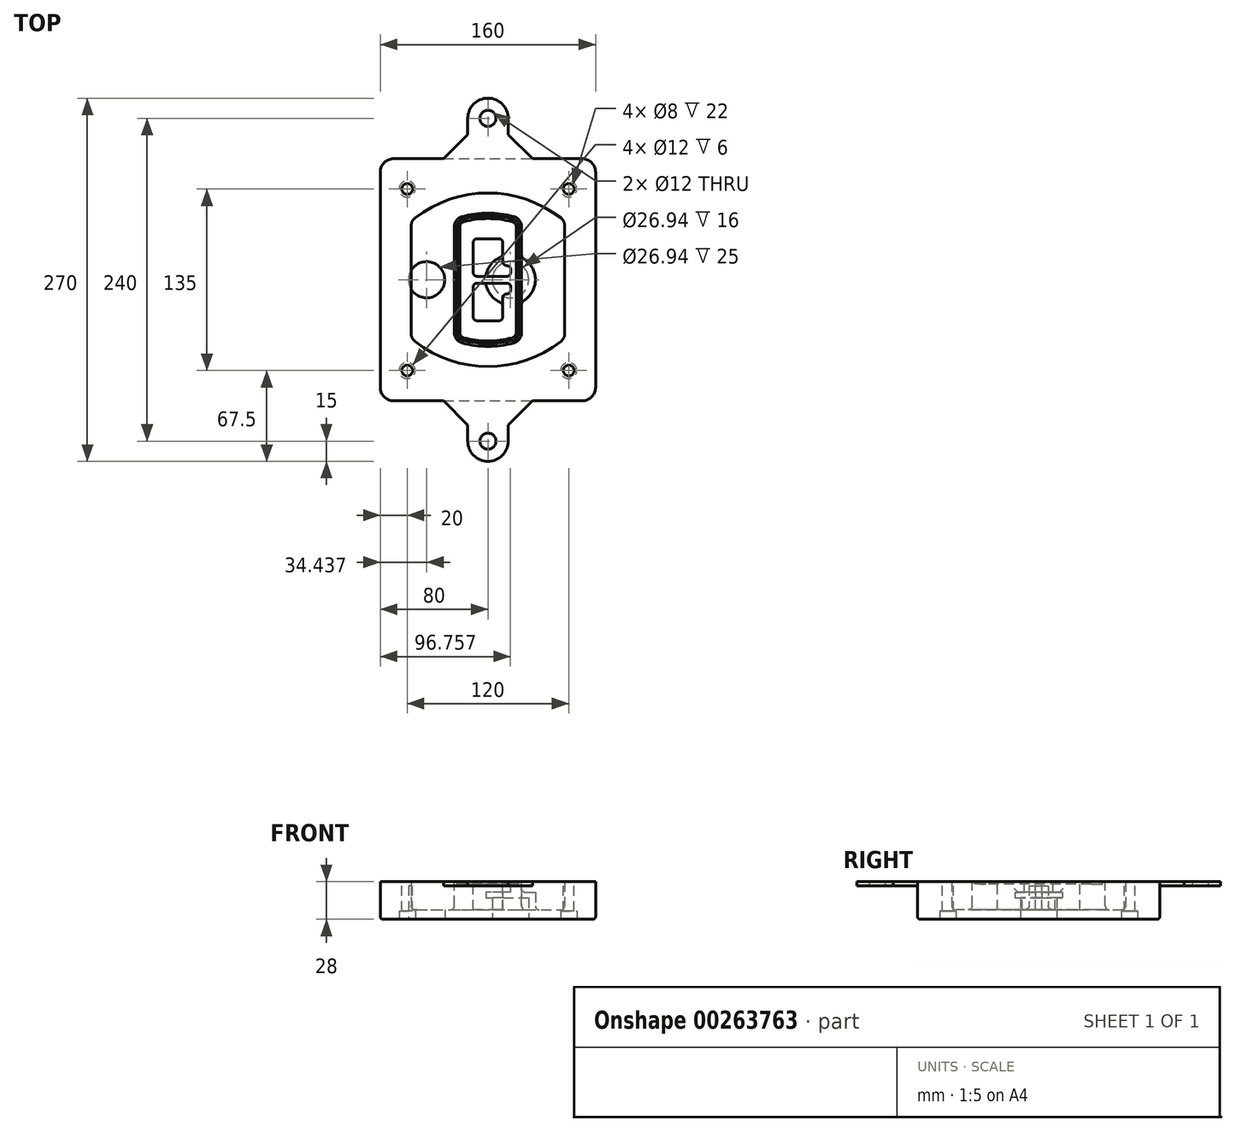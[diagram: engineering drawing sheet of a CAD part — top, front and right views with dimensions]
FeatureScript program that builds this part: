
annotation { "Feature Type Name" : "Feature", "Feature Type Description" : "" }
export const myFeature = defineFeature(function(context is Context, id is Id, definition is map)
    precondition{}
    {
        {
            var Q0;
            Q0=qCreatedBy(makeId("Top.planeOp"),FACE);
            var sketch = newSketch(context, id + "F0", { "sketchPlane" : qUnion([Q0])});
            skPoint(sketch, "E0.rect.middle", {"position": v(0, 0) * mm});
            skLineSegment(sketch, "E1.bottom", {"start": v(-70, -90) * mm, "end": v(70, -90) * mm});
            skLineSegment(sketch, "E1.top", {"start": v(-70, 90) * mm, "end": v(70, 90) * mm});
            skLineSegment(sketch, "E1.left", {"start": v(-80, -80) * mm, "end": v(-80, 80) * mm});
            skLineSegment(sketch, "E1.right", {"start": v(80, -80) * mm, "end": v(80, 80) * mm});
            skLineSegment(sketch, "E2", {"start": v(-80, 90) * mm, "end": v(80, -90) * mm, "construction": true});
            skLineSegment(sketch, "E3", {"start": v(80, 90) * mm, "end": v(-80, -90) * mm, "construction": true});
            skCircle(sketch, "E4", {"center": v(-60, 67.5) * mm, "radius": 4 * mm});
            skCircle(sketch, "E5", {"center": v(60, 67.5) * mm, "radius": 4 * mm});
            skCircle(sketch, "E6", {"center": v(60, -67.5) * mm, "radius": 4 * mm});
            skCircle(sketch, "E7", {"center": v(-60, -67.5) * mm, "radius": 4 * mm});
            skLineSegment(sketch, "E8", {"start": v(-60, 67.5) * mm, "end": v(60, 67.5) * mm, "construction": true});
            skLineSegment(sketch, "E9", {"start": v(60, 67.5) * mm, "end": v(60, -67.5) * mm, "construction": true});
            skLineSegment(sketch, "E10", {"start": v(60, -67.5) * mm, "end": v(-60, -67.5) * mm, "construction": true});
            skLineSegment(sketch, "E11", {"start": v(-60, -67.5) * mm, "end": v(-60, 67.5) * mm, "construction": true});
            skLineSegment(sketch, "E12", {"start": v(-60, 40.3) * mm, "end": v(-60, -40.3) * mm});
            skLineSegment(sketch, "E13", {"start": v(60, 40.3) * mm, "end": v(60, -40.3) * mm});
            skArc(sketch, "E14", {"start": v(56.15, 48.18) * mm, "mid": v(0, 67.5) * mm, "end": v(-56.15, 48.18) * mm});
            skArc(sketch, "E15", {"start": v(-56.15, -48.18) * mm, "mid": v(0, -67.5) * mm, "end": v(56.15, -48.18) * mm});
            skLineSegment(sketch, "E16", {"start": v(-60, 0) * mm, "end": v(60, 0) * mm, "construction": true});
            skPoint(sketch, "E17.visualSharp", {"position": v(-60, -45) * mm});
            skArc(sketch, "E17.filletArc", {"start": v(-60, -40.3) * mm, "mid": v(-58.99, -44.68) * mm, "end": v(-56.15, -48.18) * mm});
            skPoint(sketch, "E18.visualSharp", {"position": v(-60, 45) * mm});
            skArc(sketch, "E18.filletArc", {"start": v(-56.15, 48.18) * mm, "mid": v(-58.99, 44.68) * mm, "end": v(-60, 40.3) * mm});
            skPoint(sketch, "E19.visualSharp", {"position": v(60, 45) * mm});
            skArc(sketch, "E19.filletArc", {"start": v(60, 40.3) * mm, "mid": v(58.99, 44.68) * mm, "end": v(56.15, 48.18) * mm});
            skPoint(sketch, "E20.visualSharp", {"position": v(60, -45) * mm});
            skArc(sketch, "E20.filletArc", {"start": v(56.15, -48.18) * mm, "mid": v(58.99, -44.68) * mm, "end": v(60, -40.3) * mm});
            skPoint(sketch, "E21.visualSharp", {"position": v(-80, 90) * mm});
            skArc(sketch, "E21.filletArc", {"start": v(-70, 90) * mm, "mid": v(-77.07, 87.07) * mm, "end": v(-80, 80) * mm});
            skPoint(sketch, "E22.visualSharp", {"position": v(80, 90) * mm});
            skArc(sketch, "E22.filletArc", {"start": v(80, 80) * mm, "mid": v(77.07, 87.07) * mm, "end": v(70, 90) * mm});
            skPoint(sketch, "E23.visualSharp", {"position": v(80, -90) * mm});
            skArc(sketch, "E23.filletArc", {"start": v(70, -90) * mm, "mid": v(77.07, -87.07) * mm, "end": v(80, -80) * mm});
            skPoint(sketch, "E24.visualSharp", {"position": v(-80, -90) * mm});
            skArc(sketch, "E24.filletArc", {"start": v(-80, -80) * mm, "mid": v(-77.07, -87.07) * mm, "end": v(-70, -90) * mm});
            skArc(sketch, "E25.0", {"start": v(57, 40.3) * mm, "mid": v(56.3, 43.36) * mm, "end": v(54.3, 45.81) * mm});
            skLineSegment(sketch, "E25.1", {"start": v(57, 40.3) * mm, "end": v(57, -40.3) * mm});
            skArc(sketch, "E25.2", {"start": v(54.3, -45.81) * mm, "mid": v(56.3, -43.36) * mm, "end": v(57, -40.3) * mm});
            skArc(sketch, "E25.3", {"start": v(-54.3, -45.81) * mm, "mid": v(0, -64.5) * mm, "end": v(54.3, -45.81) * mm});
            skArc(sketch, "E25.4", {"start": v(-57, -40.3) * mm, "mid": v(-56.3, -43.36) * mm, "end": v(-54.3, -45.81) * mm});
            skArc(sketch, "E25.5", {"start": v(54.3, 45.81) * mm, "mid": v(0, 64.5) * mm, "end": v(-54.3, 45.81) * mm});
            skLineSegment(sketch, "E25.6", {"start": v(-57, 40.3) * mm, "end": v(-57, -40.3) * mm});
            skArc(sketch, "E25.7", {"start": v(-54.3, 45.81) * mm, "mid": v(-56.3, 43.36) * mm, "end": v(-57, 40.3) * mm});
            skArc(sketch, "E26.0", {"start": v(-58.62, 51.33) * mm, "mid": v(-62.58, 46.43) * mm, "end": v(-64, 40.3) * mm});
            skArc(sketch, "E26.1", {"start": v(58.62, 51.33) * mm, "mid": v(0, 71.5) * mm, "end": v(-58.62, 51.33) * mm});
            skArc(sketch, "E26.2", {"start": v(64, 40.3) * mm, "mid": v(62.58, 46.43) * mm, "end": v(58.62, 51.33) * mm});
            skLineSegment(sketch, "E26.3", {"start": v(64, 40.3) * mm, "end": v(64, -40.3) * mm});
            skArc(sketch, "E26.4", {"start": v(58.62, -51.33) * mm, "mid": v(62.58, -46.43) * mm, "end": v(64, -40.3) * mm});
            skLineSegment(sketch, "E26.5", {"start": v(-64, 40.3) * mm, "end": v(-64, -40.3) * mm});
            skArc(sketch, "E26.6", {"start": v(-58.62, -51.33) * mm, "mid": v(0, -71.5) * mm, "end": v(58.62, -51.33) * mm});
            skArc(sketch, "E26.7", {"start": v(-64, -40.3) * mm, "mid": v(-62.58, -46.43) * mm, "end": v(-58.62, -51.33) * mm});
            skSolve(sketch);
        }
        {
            var Q0;
            Q0=makeQuery(id+"F0.imprint","IMPRINT",FACE,{"disambiguationData":[TD([[makeQuery(id+"F0.imprint","IMPRINT",EDGE,{"derivedFrom":sQuery(id+"F0.wireOp",EDGE,"E1.bottom")}),1.0]])]});
            var Q1;
            Q1=makeQuery(id+"F0.imprint","IMPRINT",FACE,{"disambiguationData":[TD([[makeQuery(id+"F0.imprint","IMPRINT",EDGE,{"derivedFrom":sQuery(id+"F0.wireOp",EDGE,"E12")}),1.0]])]});
            var Q2;
            Q2=makeQuery(id+"F0.imprint","IMPRINT",FACE,{"disambiguationData":[TD([[makeQuery(id+"F0.imprint","IMPRINT",EDGE,{"derivedFrom":sQuery(id+"F0.wireOp",EDGE,"E25.0")}),1.0]])]});
            var Q3;
            Q3=makeQuery(id+"F0.imprint","IMPRINT",FACE,{"disambiguationData":[TD([[makeQuery(id+"F0.imprint","IMPRINT",EDGE,{"derivedFrom":sQuery(id+"F0.wireOp",EDGE,"E12")}),-1.0]])]});
            extrude(context, id + "F1", {"entities" : qUnion([Q0, Q1, Q2, Q3]), "oppositeDirection" : true, "depth" : 25 * mm});
        }
        {
            var Q0;
            Q0=makeQuery(id+"F0.imprint","IMPRINT",FACE,{"disambiguationData":[TD([[makeQuery(id+"F0.imprint","IMPRINT",EDGE,{"derivedFrom":sQuery(id+"F0.wireOp",EDGE,"E12")}),1.0]])]});
            extrude(context, id + "F2", {"entities" : qUnion([Q0]), "operationType" : NewBodyOperationType.ADD, "depth" : 3 * mm});
        }
        {
            var Q0;
            Q0=makeQuery(id+"F0.imprint","IMPRINT",FACE,{"disambiguationData":[TD([[makeQuery(id+"F0.imprint","IMPRINT",EDGE,{"derivedFrom":sQuery(id+"F0.wireOp",EDGE,"E25.0")}),1.0]])]});
            extrude(context, id + "F3", {"entities" : qUnion([Q0]), "operationType" : NewBodyOperationType.REMOVE, "oppositeDirection" : true, "depth" : 18 * mm});
        }
        {
            var Q0;
            Q0=makeQuery(id+"F2.opExtrude","CAP_FACE",FACE,{"disambiguationData":[OSD([sQuery(id+"F0.wireOp",EDGE,"E12"),sQuery(id+"F0.wireOp",EDGE,"E13"),sQuery(id+"F0.wireOp",EDGE,"E14"),sQuery(id+"F0.wireOp",EDGE,"E15"),sQuery(id+"F0.wireOp",EDGE,"E17.filletArc"),sQuery(id+"F0.wireOp",EDGE,"E18.filletArc"),sQuery(id+"F0.wireOp",EDGE,"E19.filletArc"),sQuery(id+"F0.wireOp",EDGE,"E20.filletArc"),sQuery(id+"F0.wireOp",EDGE,"E25.0"),sQuery(id+"F0.wireOp",EDGE,"E25.1"),sQuery(id+"F0.wireOp",EDGE,"E25.2"),sQuery(id+"F0.wireOp",EDGE,"E25.3"),sQuery(id+"F0.wireOp",EDGE,"E25.4"),sQuery(id+"F0.wireOp",EDGE,"E25.5"),sQuery(id+"F0.wireOp",EDGE,"E25.6"),sQuery(id+"F0.wireOp",EDGE,"E25.7")])],"isStart":false});
            var sketch = newSketch(context, id + "F4", { "sketchPlane" : qUnion([Q0])});
            skArc(sketch, "E27.0", {"start": v(-19.08, -46.97) * mm, "mid": v(0, -49.5) * mm, "end": v(19.08, -46.97) * mm});
            skArc(sketch, "E28.0", {"start": v(19.08, 46.97) * mm, "mid": v(0, 49.5) * mm, "end": v(-19.08, 46.97) * mm});
            skLineSegment(sketch, "E29", {"start": v(-25, 39.25) * mm, "end": v(-25, -39.25) * mm});
            skLineSegment(sketch, "E30", {"start": v(25, 39.25) * mm, "end": v(25, -39.25) * mm});
            skLineSegment(sketch, "E31", {"start": v(-25, 45.1) * mm, "end": v(25, 45.1) * mm, "construction": true});
            skLineSegment(sketch, "E32", {"start": v(-25, -45.1) * mm, "end": v(25, -45.1) * mm, "construction": true});
            skPoint(sketch, "E33.visualSharp", {"position": v(-25, 45.1) * mm});
            skArc(sketch, "E33.filletArc", {"start": v(-19.08, 46.97) * mm, "mid": v(-23.35, 44.11) * mm, "end": v(-25, 39.25) * mm});
            skPoint(sketch, "E34.visualSharp", {"position": v(25, 45.1) * mm});
            skArc(sketch, "E34.filletArc", {"start": v(25, 39.25) * mm, "mid": v(23.35, 44.11) * mm, "end": v(19.08, 46.97) * mm});
            skPoint(sketch, "E35.visualSharp", {"position": v(25, -45.1) * mm});
            skArc(sketch, "E35.filletArc", {"start": v(19.08, -46.97) * mm, "mid": v(23.35, -44.11) * mm, "end": v(25, -39.25) * mm});
            skPoint(sketch, "E36.visualSharp", {"position": v(-25, -45.1) * mm});
            skArc(sketch, "E36.filletArc", {"start": v(-25, -39.25) * mm, "mid": v(-23.35, -44.11) * mm, "end": v(-19.08, -46.97) * mm});
            skArc(sketch, "E37.0", {"start": v(54.3, 45.81) * mm, "mid": v(0, 64.5) * mm, "end": v(-54.3, 45.81) * mm});
            skArc(sketch, "E37.1", {"start": v(-54.3, 45.81) * mm, "mid": v(-56.3, 43.36) * mm, "end": v(-57, 40.3) * mm});
            skLineSegment(sketch, "E37.2", {"start": v(-57, 40.3) * mm, "end": v(-57, -40.3) * mm});
            skArc(sketch, "E37.3", {"start": v(-57, -40.3) * mm, "mid": v(-56.3, -43.36) * mm, "end": v(-54.3, -45.81) * mm});
            skArc(sketch, "E37.4", {"start": v(-54.3, -45.81) * mm, "mid": v(0, -64.5) * mm, "end": v(54.3, -45.81) * mm});
            skArc(sketch, "E37.5", {"start": v(54.3, -45.81) * mm, "mid": v(56.3, -43.36) * mm, "end": v(57, -40.3) * mm});
            skLineSegment(sketch, "E37.6", {"start": v(57, 40.3) * mm, "end": v(57, -40.3) * mm});
            skArc(sketch, "E37.7", {"start": v(57, 40.3) * mm, "mid": v(56.3, 43.36) * mm, "end": v(54.3, 45.81) * mm});
            skLineSegment(sketch, "E38.0", {"start": v(23, 39.25) * mm, "end": v(23, -39.25) * mm});
            skArc(sketch, "E38.1", {"start": v(18.56, -45.04) * mm, "mid": v(21.76, -42.9) * mm, "end": v(23, -39.25) * mm});
            skArc(sketch, "E38.2", {"start": v(-18.56, -45.04) * mm, "mid": v(0, -47.5) * mm, "end": v(18.56, -45.04) * mm});
            skArc(sketch, "E38.3", {"start": v(-23, -39.25) * mm, "mid": v(-21.76, -42.9) * mm, "end": v(-18.56, -45.04) * mm});
            skLineSegment(sketch, "E38.4", {"start": v(-23, 39.25) * mm, "end": v(-23, -39.25) * mm});
            skArc(sketch, "E38.5", {"start": v(23, 39.25) * mm, "mid": v(21.76, 42.9) * mm, "end": v(18.56, 45.04) * mm});
            skArc(sketch, "E38.6", {"start": v(-18.56, 45.04) * mm, "mid": v(-21.76, 42.9) * mm, "end": v(-23, 39.25) * mm});
            skArc(sketch, "E38.7", {"start": v(18.56, 45.04) * mm, "mid": v(0, 47.5) * mm, "end": v(-18.56, 45.04) * mm});
            skArc(sketch, "E39.0", {"start": v(21, 39.25) * mm, "mid": v(20.18, 41.68) * mm, "end": v(18.04, 43.1) * mm});
            skLineSegment(sketch, "E39.1", {"start": v(21, 39.25) * mm, "end": v(21, -39.25) * mm});
            skArc(sketch, "E39.2", {"start": v(18.04, -43.1) * mm, "mid": v(20.18, -41.68) * mm, "end": v(21, -39.25) * mm});
            skArc(sketch, "E39.3", {"start": v(-18.04, -43.1) * mm, "mid": v(0, -45.5) * mm, "end": v(18.04, -43.1) * mm});
            skArc(sketch, "E39.4", {"start": v(-21, -39.25) * mm, "mid": v(-20.18, -41.68) * mm, "end": v(-18.04, -43.1) * mm});
            skArc(sketch, "E39.5", {"start": v(18.04, 43.1) * mm, "mid": v(0, 45.5) * mm, "end": v(-18.04, 43.1) * mm});
            skLineSegment(sketch, "E39.6", {"start": v(-21, 39.25) * mm, "end": v(-21, -39.25) * mm});
            skArc(sketch, "E39.7", {"start": v(-18.04, 43.1) * mm, "mid": v(-20.18, 41.68) * mm, "end": v(-21, 39.25) * mm});
            skLineSegment(sketch, "E40", {"start": v(-25, 0) * mm, "end": v(25, 0) * mm, "construction": true});
            skLineSegment(sketch, "E41", {"start": v(-11, 5.5) * mm, "end": v(-11, 27.5) * mm});
            skLineSegment(sketch, "E42", {"start": v(-8, 30.5) * mm, "end": v(8, 30.5) * mm});
            skLineSegment(sketch, "E43", {"start": v(11, 27.5) * mm, "end": v(11, 13.5) * mm});
            skLineSegment(sketch, "E44", {"start": v(14, 10.5) * mm, "end": v(14, 10.5) * mm});
            skLineSegment(sketch, "E45", {"start": v(17, 7.5) * mm, "end": v(17, 5.5) * mm});
            skLineSegment(sketch, "E46", {"start": v(14, 2.5) * mm, "end": v(-8, 2.5) * mm});
            skPoint(sketch, "E47.visualSharp", {"position": v(-11, 30.5) * mm});
            skArc(sketch, "E47.filletArc", {"start": v(-8, 30.5) * mm, "mid": v(-10.12, 29.62) * mm, "end": v(-11, 27.5) * mm});
            skPoint(sketch, "E48.visualSharp", {"position": v(11, 30.5) * mm});
            skArc(sketch, "E48.filletArc", {"start": v(11, 27.5) * mm, "mid": v(10.12, 29.62) * mm, "end": v(8, 30.5) * mm});
            skPoint(sketch, "E49.visualSharp", {"position": v(11, 10.5) * mm});
            skArc(sketch, "E49.filletArc", {"start": v(11, 13.5) * mm, "mid": v(11.88, 11.38) * mm, "end": v(14, 10.5) * mm});
            skPoint(sketch, "E50.visualSharp", {"position": v(17, 10.5) * mm});
            skArc(sketch, "E50.filletArc", {"start": v(17, 7.5) * mm, "mid": v(16.12, 9.62) * mm, "end": v(14, 10.5) * mm});
            skPoint(sketch, "E51.visualSharp", {"position": v(17, 2.5) * mm});
            skArc(sketch, "E51.filletArc", {"start": v(14, 2.5) * mm, "mid": v(16.12, 3.38) * mm, "end": v(17, 5.5) * mm});
            skPoint(sketch, "E52.visualSharp", {"position": v(-11, 2.5) * mm});
            skArc(sketch, "E52.filletArc", {"start": v(-11, 5.5) * mm, "mid": v(-10.12, 3.38) * mm, "end": v(-8, 2.5) * mm});
            skLineSegment(sketch, "E53.0.MirrorCS", {"start": v(14, -2.5) * mm, "end": v(-8, -2.5) * mm});
            skArc(sketch, "E54.0.MirrorCS", {"start": v(-11, -5.5) * mm, "mid": v(-10.12, -3.38) * mm, "end": v(-8, -2.5) * mm});
            skLineSegment(sketch, "E55.0.MirrorCS", {"start": v(-11, -5.5) * mm, "end": v(-11, -27.5) * mm});
            skArc(sketch, "E56.0.MirrorCS", {"start": v(-8, -30.5) * mm, "mid": v(-10.12, -29.62) * mm, "end": v(-11, -27.5) * mm});
            skLineSegment(sketch, "E57.0.MirrorCS", {"start": v(-8, -30.5) * mm, "end": v(8, -30.5) * mm});
            skArc(sketch, "E58.0.MirrorCS", {"start": v(11, -27.5) * mm, "mid": v(10.12, -29.62) * mm, "end": v(8, -30.5) * mm});
            skLineSegment(sketch, "E59.0.MirrorCS", {"start": v(11, -27.5) * mm, "end": v(11, -13.5) * mm});
            skArc(sketch, "E60.0.MirrorCS", {"start": v(11, -13.5) * mm, "mid": v(11.88, -11.38) * mm, "end": v(14, -10.5) * mm});
            skArc(sketch, "E61.0.MirrorCS", {"start": v(17, -7.5) * mm, "mid": v(16.12, -9.62) * mm, "end": v(14, -10.5) * mm});
            skLineSegment(sketch, "E62.0.MirrorCS", {"start": v(17, -7.5) * mm, "end": v(17, -5.5) * mm});
            skArc(sketch, "E63.0.MirrorCS", {"start": v(14, -2.5) * mm, "mid": v(16.12, -3.38) * mm, "end": v(17, -5.5) * mm});
            skSolve(sketch);
        }
        {
            var Q0;
            Q0=makeQuery(id+"F4.imprint","IMPRINT",FACE,{"disambiguationData":[TD([[makeQuery(id+"F4.imprint","IMPRINT",EDGE,{"derivedFrom":sQuery(id+"F4.wireOp",EDGE,"E27.0")}),1.0]])]});
            var Q1;
            Q1=makeQuery(id+"F4.imprint","IMPRINT",FACE,{"disambiguationData":[TD([[makeQuery(id+"F4.imprint","IMPRINT",EDGE,{"derivedFrom":sQuery(id+"F4.wireOp",EDGE,"E38.0")}),-1.0]])]});
            var Q2;
            Q2=makeQuery(id+"F4.imprint","IMPRINT",FACE,{"disambiguationData":[TD([[makeQuery(id+"F4.imprint","IMPRINT",EDGE,{"derivedFrom":sQuery(id+"F4.wireOp",EDGE,"E39.0")}),1.0]])]});
            extrude(context, id + "F5", {"entities" : qUnion([Q0, Q1, Q2]), "operationType" : NewBodyOperationType.ADD, "endBound" : BoundingType.UP_TO_NEXT, "oppositeDirection" : true, "depth" : 25 * mm});
        }
        {
            var Q0;
            Q0=makeQuery(id+"F4.imprint","IMPRINT",FACE,{"disambiguationData":[TD([[makeQuery(id+"F4.imprint","IMPRINT",EDGE,{"derivedFrom":sQuery(id+"F4.wireOp",EDGE,"E38.0")}),-1.0]])]});
            extrude(context, id + "F6", {"entities" : qUnion([Q0]), "operationType" : NewBodyOperationType.REMOVE, "oppositeDirection" : true, "depth" : 2 * mm});
        }
        {
            var Q0;
            Q0=makeQuery(id+"F1.opExtrude","CAP_FACE",FACE,{"disambiguationData":[OSD([sQuery(id+"F0.wireOp",EDGE,"E1.bottom"),sQuery(id+"F0.wireOp",EDGE,"E1.top"),sQuery(id+"F0.wireOp",EDGE,"E1.left"),sQuery(id+"F0.wireOp",EDGE,"E1.right"),sQuery(id+"F0.wireOp",EDGE,"E4"),sQuery(id+"F0.wireOp",EDGE,"E5"),sQuery(id+"F0.wireOp",EDGE,"E6"),sQuery(id+"F0.wireOp",EDGE,"E7"),sQuery(id+"F0.wireOp",EDGE,"E21.filletArc"),sQuery(id+"F0.wireOp",EDGE,"E22.filletArc"),sQuery(id+"F0.wireOp",EDGE,"E23.filletArc"),sQuery(id+"F0.wireOp",EDGE,"E24.filletArc")])],"isStart":false});
            var sketch = newSketch(context, id + "F7", { "sketchPlane" : qUnion([Q0])});
            skCircle(sketch, "E64", {"center": v(16.76, 0) * mm, "radius": 13.47 * mm});
            skCircle(sketch, "E65", {"center": v(-45.56, 0) * mm, "radius": 13.47 * mm});
            skLineSegment(sketch, "E66", {"start": v(80, 0) * mm, "end": v(-80, 0) * mm});
            skCircle(sketch, "E67", {"center": v(16.76, 0) * mm, "radius": 18.47 * mm});
            skCircle(sketch, "E68", {"center": v(60, -67.5) * mm, "radius": 6 * mm});
            skCircle(sketch, "E69", {"center": v(-60, -67.5) * mm, "radius": 6 * mm});
            skCircle(sketch, "E70", {"center": v(-60, 67.5) * mm, "radius": 6 * mm});
            skCircle(sketch, "E71", {"center": v(60, 67.5) * mm, "radius": 6 * mm});
            skSolve(sketch);
        }
        {
            var Q0;
            {var subQ1=sQuery(id+"F7.wireOp",EDGE,"E66");var subQ4=sQuery(id+"F7.wireOp",EDGE,"E64");var subQ6=makeQuery(id+"F7.imprint","INTERSECT",VERTEX,{"disambiguationData":[OD(0.0)],"derivedFrom":[subQ4,subQ1]});Q0=makeQuery(id+"F7.imprint","IMPRINT",FACE,{"disambiguationData":[TD([[makeQuery(id+"F7.imprint","IMPRINT",EDGE,{"disambiguationData":[TD([[subQ6,-1.0]])],"derivedFrom":subQ4}),-1.0]])]});}
            var Q1;
            {var subQ0=sQuery(id+"F7.wireOp",EDGE,"E66");var subQ1=sQuery(id+"F7.wireOp",EDGE,"E64");var subQ3=makeQuery(id+"F7.imprint","INTERSECT",VERTEX,{"disambiguationData":[OD(0.0)],"derivedFrom":[subQ1,subQ0]});Q1=makeQuery(id+"F7.imprint","IMPRINT",FACE,{"disambiguationData":[TD([[makeQuery(id+"F7.imprint","IMPRINT",EDGE,{"disambiguationData":[TD([[subQ3,-1.0]])],"derivedFrom":subQ1}),1.0]])]});}
            var Q2;
            {var subQ0=sQuery(id+"F7.wireOp",EDGE,"E66");var subQ1=sQuery(id+"F7.wireOp",EDGE,"E64");var subQ3=makeQuery(id+"F7.imprint","INTERSECT",VERTEX,{"disambiguationData":[OD(0.0)],"derivedFrom":[subQ1,subQ0]});Q2=makeQuery(id+"F7.imprint","IMPRINT",FACE,{"disambiguationData":[TD([[makeQuery(id+"F7.imprint","IMPRINT",EDGE,{"disambiguationData":[TD([[subQ3,1.0]])],"derivedFrom":subQ1}),1.0]])]});}
            var Q3;
            {var subQ1=sQuery(id+"F7.wireOp",EDGE,"E66");var subQ4=sQuery(id+"F7.wireOp",EDGE,"E64");var subQ6=makeQuery(id+"F7.imprint","INTERSECT",VERTEX,{"disambiguationData":[OD(0.0)],"derivedFrom":[subQ4,subQ1]});Q3=makeQuery(id+"F7.imprint","IMPRINT",FACE,{"disambiguationData":[TD([[makeQuery(id+"F7.imprint","IMPRINT",EDGE,{"disambiguationData":[TD([[subQ6,1.0]])],"derivedFrom":subQ4}),-1.0]])]});}
            extrude(context, id + "F8", {"entities" : qUnion([Q0, Q1, Q2, Q3]), "operationType" : NewBodyOperationType.ADD, "oppositeDirection" : true, "depth" : 20 * mm});
        }
        {
            var Q0;
            {var subQ0=sQuery(id+"F7.wireOp",EDGE,"E66");var subQ1=sQuery(id+"F7.wireOp",EDGE,"E64");var subQ3=makeQuery(id+"F7.imprint","INTERSECT",VERTEX,{"disambiguationData":[OD(0.0)],"derivedFrom":[subQ1,subQ0]});Q0=makeQuery(id+"F7.imprint","IMPRINT",FACE,{"disambiguationData":[TD([[makeQuery(id+"F7.imprint","IMPRINT",EDGE,{"disambiguationData":[TD([[subQ3,-1.0]])],"derivedFrom":subQ1}),1.0]])]});}
            var Q1;
            {var subQ0=sQuery(id+"F7.wireOp",EDGE,"E66");var subQ1=sQuery(id+"F7.wireOp",EDGE,"E64");var subQ3=makeQuery(id+"F7.imprint","INTERSECT",VERTEX,{"disambiguationData":[OD(0.0)],"derivedFrom":[subQ1,subQ0]});Q1=makeQuery(id+"F7.imprint","IMPRINT",FACE,{"disambiguationData":[TD([[makeQuery(id+"F7.imprint","IMPRINT",EDGE,{"disambiguationData":[TD([[subQ3,1.0]])],"derivedFrom":subQ1}),1.0]])]});}
            extrude(context, id + "F9", {"entities" : qUnion([Q0, Q1]), "operationType" : NewBodyOperationType.REMOVE, "oppositeDirection" : true, "depth" : 16 * mm});
        }
        {
            var Q0;
            {var subQ0=sQuery(id+"F7.wireOp",EDGE,"E66");var subQ1=sQuery(id+"F7.wireOp",EDGE,"E65");var subQ3=makeQuery(id+"F7.imprint","INTERSECT",VERTEX,{"disambiguationData":[OD(0.0)],"derivedFrom":[subQ1,subQ0]});Q0=makeQuery(id+"F7.imprint","IMPRINT",FACE,{"disambiguationData":[TD([[makeQuery(id+"F7.imprint","IMPRINT",EDGE,{"disambiguationData":[TD([[subQ3,-1.0]])],"derivedFrom":subQ1}),1.0]])]});}
            var Q1;
            {var subQ0=sQuery(id+"F7.wireOp",EDGE,"E66");var subQ1=sQuery(id+"F7.wireOp",EDGE,"E65");var subQ3=makeQuery(id+"F7.imprint","INTERSECT",VERTEX,{"disambiguationData":[OD(0.0)],"derivedFrom":[subQ1,subQ0]});Q1=makeQuery(id+"F7.imprint","IMPRINT",FACE,{"disambiguationData":[TD([[makeQuery(id+"F7.imprint","IMPRINT",EDGE,{"disambiguationData":[TD([[subQ3,1.0]])],"derivedFrom":subQ1}),1.0]])]});}
            extrude(context, id + "F10", {"entities" : qUnion([Q0, Q1]), "operationType" : NewBodyOperationType.REMOVE, "oppositeDirection" : true, "depth" : 25 * mm});
        }
        {
            var Q0;
            Q0=makeQuery(id+"F7.imprint","IMPRINT",FACE,{"disambiguationData":[TD([[makeQuery(id+"F7.imprint","IMPRINT",EDGE,{"derivedFrom":sQuery(id+"F7.wireOp",EDGE,"E68")}),1.0]])]});
            var Q1;
            Q1=makeQuery(id+"F7.imprint","IMPRINT",FACE,{"disambiguationData":[TD([[makeQuery(id+"F7.imprint","IMPRINT",EDGE,{"derivedFrom":makeQuery(id+"F1.opExtrude","CAP_EDGE",EDGE,{"disambiguationData":[OSD([sQuery(id+"F0.wireOp",EDGE,"E5")])],"isStart":false})}),-1.0]])]});
            var Q2;
            Q2=makeQuery(id+"F7.imprint","IMPRINT",FACE,{"disambiguationData":[TD([[makeQuery(id+"F7.imprint","IMPRINT",EDGE,{"derivedFrom":sQuery(id+"F7.wireOp",EDGE,"E69")}),1.0]])]});
            var Q3;
            Q3=makeQuery(id+"F7.imprint","IMPRINT",FACE,{"disambiguationData":[TD([[makeQuery(id+"F7.imprint","IMPRINT",EDGE,{"derivedFrom":makeQuery(id+"F1.opExtrude","CAP_EDGE",EDGE,{"disambiguationData":[OSD([sQuery(id+"F0.wireOp",EDGE,"E4")])],"isStart":false})}),-1.0]])]});
            var Q4;
            Q4=makeQuery(id+"F7.imprint","IMPRINT",FACE,{"disambiguationData":[TD([[makeQuery(id+"F7.imprint","IMPRINT",EDGE,{"derivedFrom":sQuery(id+"F7.wireOp",EDGE,"E70")}),1.0]])]});
            var Q5;
            Q5=makeQuery(id+"F7.imprint","IMPRINT",FACE,{"disambiguationData":[TD([[makeQuery(id+"F7.imprint","IMPRINT",EDGE,{"derivedFrom":makeQuery(id+"F1.opExtrude","CAP_EDGE",EDGE,{"disambiguationData":[OSD([sQuery(id+"F0.wireOp",EDGE,"E7")])],"isStart":false})}),-1.0]])]});
            var Q6;
            Q6=makeQuery(id+"F7.imprint","IMPRINT",FACE,{"disambiguationData":[TD([[makeQuery(id+"F7.imprint","IMPRINT",EDGE,{"derivedFrom":sQuery(id+"F7.wireOp",EDGE,"E71")}),1.0]])]});
            var Q7;
            Q7=makeQuery(id+"F7.imprint","IMPRINT",FACE,{"disambiguationData":[TD([[makeQuery(id+"F7.imprint","IMPRINT",EDGE,{"derivedFrom":makeQuery(id+"F1.opExtrude","CAP_EDGE",EDGE,{"disambiguationData":[OSD([sQuery(id+"F0.wireOp",EDGE,"E6")])],"isStart":false})}),-1.0]])]});
            extrude(context, id + "F11", {"entities" : qUnion([Q0, Q1, Q2, Q3, Q4, Q5, Q6, Q7]), "operationType" : NewBodyOperationType.REMOVE, "oppositeDirection" : true, "depth" : 6 * mm});
        }
        {
            var Q0;
            Q0=makeQuery(id+"F9.boolean.opBoolean","COPY",FACE,{"derivedFrom":makeQuery(id+"F9.opExtrude","CAP_FACE",FACE,{"disambiguationData":[OSD([sQuery(id+"F7.wireOp",EDGE,"E64")])],"isStart":false})});
            var sketch = newSketch(context, id + "F12", { "sketchPlane" : qUnion([Q0])});
            skArc(sketch, "E72.0", {"start": v(11, 17.55) * mm, "mid": v(2.57, 11.82) * mm, "end": v(-1.54, 2.5) * mm});
            skArc(sketch, "E72.1", {"start": v(-1.54, -2.5) * mm, "mid": v(2.57, -11.82) * mm, "end": v(11, -17.55) * mm});
            skLineSegment(sketch, "E73", {"start": v(-1.54, -2.5) * mm, "end": v(14, -2.5) * mm});
            skLineSegment(sketch, "E74.0", {"start": v(14, 2.5) * mm, "end": v(-1.54, 2.5) * mm});
            skArc(sketch, "E74.1", {"start": v(14, 2.5) * mm, "mid": v(16.12, 3.38) * mm, "end": v(17, 5.5) * mm});
            skLineSegment(sketch, "E74.2", {"start": v(17, 7.5) * mm, "end": v(17, 5.5) * mm});
            skArc(sketch, "E74.3", {"start": v(17, 7.5) * mm, "mid": v(16.12, 9.62) * mm, "end": v(14, 10.5) * mm});
            skArc(sketch, "E74.4", {"start": v(11, 13.5) * mm, "mid": v(11.88, 11.38) * mm, "end": v(14, 10.5) * mm});
            skLineSegment(sketch, "E74.5", {"start": v(11, 17.55) * mm, "end": v(11, 13.5) * mm});
            skLineSegment(sketch, "E74.7", {"start": v(14, -2.5) * mm, "end": v(-1.54, -2.5) * mm});
            skArc(sketch, "E74.8", {"start": v(14, -2.5) * mm, "mid": v(16.12, -3.38) * mm, "end": v(17, -5.5) * mm});
            skLineSegment(sketch, "E74.9", {"start": v(17, -7.5) * mm, "end": v(17, -5.5) * mm});
            skArc(sketch, "E74.10", {"start": v(17, -7.5) * mm, "mid": v(16.12, -9.62) * mm, "end": v(14, -10.5) * mm});
            skArc(sketch, "E74.11", {"start": v(11, -13.5) * mm, "mid": v(11.88, -11.38) * mm, "end": v(14, -10.5) * mm});
            skLineSegment(sketch, "E74.12", {"start": v(11, -17.55) * mm, "end": v(11, -13.5) * mm});
            skPoint(sketch, "E75.orphan", {"position": v(11, -27.5) * mm});
            skPoint(sketch, "E76.orphan", {"position": v(-8, -2.5) * mm});
            skPoint(sketch, "E77.orphan", {"position": v(-8, 2.5) * mm});
            skPoint(sketch, "E78.orphan", {"position": v(11, 27.5) * mm});
            skSolve(sketch);
        }
        {
            var Q0;
            {var subQ7=sQuery(id+"F12.wireOp",EDGE,"E72.0");var subQ14=sQuery(id+"F12.wireOp",EDGE,"E72.1");var subQ16=sQuery(id+"F12.wireOp",EDGE,"E74.1");var subQ18=sQuery(id+"F12.wireOp",EDGE,"E74.8");Q0=qUnion([makeQuery(id+"F12.imprint","IMPRINT",FACE,{"disambiguationData":[TD([[makeQuery(id+"F12.imprint","IMPRINT",EDGE,{"derivedFrom":subQ7}),1.0]])]}),makeQuery(id+"F12.imprint","IMPRINT",FACE,{"disambiguationData":[TD([[makeQuery(id+"F12.imprint","IMPRINT",EDGE,{"derivedFrom":subQ14}),1.0]])]}),makeQuery(id+"F12.imprint","IMPRINT",FACE,{"disambiguationData":[TD([[makeQuery(id+"F12.imprint","IMPRINT",EDGE,{"derivedFrom":subQ16}),1.0]])]}),makeQuery(id+"F12.imprint","IMPRINT",FACE,{"disambiguationData":[TD([[makeQuery(id+"F12.imprint","IMPRINT",EDGE,{"derivedFrom":subQ18}),-1.0]])]})]);}
            var Q1;
            Q1=makeQuery(id+"F5.boolean.opBoolean","SPLIT",FACE,{"disambiguationData":[TD([makeQuery(id+"F5.opExtrude","SWEPT_FACE",FACE,{"disambiguationData":[OSD([sQuery(id+"F4.wireOp",EDGE,"E41")])]})])],"derivedFrom":makeQuery(id+"F3.boolean.opBoolean","COPY",FACE,{"derivedFrom":makeQuery(id+"F3.opExtrude","CAP_FACE",FACE,{"disambiguationData":[OSD([sQuery(id+"F0.wireOp",EDGE,"E25.0"),sQuery(id+"F0.wireOp",EDGE,"E25.1"),sQuery(id+"F0.wireOp",EDGE,"E25.2"),sQuery(id+"F0.wireOp",EDGE,"E25.3"),sQuery(id+"F0.wireOp",EDGE,"E25.4"),sQuery(id+"F0.wireOp",EDGE,"E25.5"),sQuery(id+"F0.wireOp",EDGE,"E25.6"),sQuery(id+"F0.wireOp",EDGE,"E25.7")])],"isStart":false})})});
            extrude(context, id + "F13", {"entities" : qUnion([Q0]), "operationType" : NewBodyOperationType.REMOVE, "endBound" : BoundingType.UP_TO_SURFACE, "endBoundEntityFace" : qUnion([Q1]), "depth" : 25 * mm});
        }
        {
            var Q0;
            Q0=makeQuery(id+"F3.boolean.opBoolean","COPY",EDGE,{"derivedFrom":makeQuery(id+"F3.opExtrude","CAP_EDGE",EDGE,{"disambiguationData":[OSD([sQuery(id+"F0.wireOp",EDGE,"E25.6")])],"isStart":false})});
            var Q1;
            Q1=makeQuery(id+"F8.boolean.opBoolean","INTERSECT",EDGE,{"derivedFrom":[makeQuery(id+"F5.opExtrude","SWEPT_FACE",FACE,{"disambiguationData":[OSD([sQuery(id+"F4.wireOp",EDGE,"E30")])]}),makeQuery(id+"F8.opExtrude","CAP_FACE",FACE,{"disambiguationData":[OSD([sQuery(id+"F7.wireOp",EDGE,"E67")])],"isStart":false})]});
            var Q2;
            Q2=makeQuery(id+"F8.boolean.opBoolean","INTERSECT",EDGE,{"disambiguationData":[OD(1.0)],"derivedFrom":[makeQuery(id+"F5.opExtrude","SWEPT_FACE",FACE,{"disambiguationData":[OSD([sQuery(id+"F4.wireOp",EDGE,"E30")])]}),makeQuery(id+"F8.opExtrude","SWEPT_FACE",FACE,{"disambiguationData":[OSD([sQuery(id+"F7.wireOp",EDGE,"E67")])]})]});
            var Q3;
            {var subQ0=sQuery(id+"F4.wireOp",EDGE,"E30");Q3=makeQuery(id+"F8.boolean.opBoolean","SPLIT",EDGE,{"disambiguationData":[TD([makeQuery(id+"F5.opExtrude","SWEPT_FACE",FACE,{"disambiguationData":[OSD([sQuery(id+"F4.wireOp",EDGE,"E35.filletArc")])]})])],"derivedFrom":makeQuery(id+"F5.opExtrude","CAP_EDGE",EDGE,{"disambiguationData":[OSD([subQ0])],"isStart":false})});}
            var Q4;
            {var subQ0=sQuery(id+"F0.wireOp",EDGE,"E25.7");var subQ1=sQuery(id+"F0.wireOp",EDGE,"E25.1");var subQ2=sQuery(id+"F0.wireOp",EDGE,"E25.6");var subQ3=sQuery(id+"F0.wireOp",EDGE,"E25.5");var subQ4=sQuery(id+"F0.wireOp",EDGE,"E25.4");var subQ5=sQuery(id+"F0.wireOp",EDGE,"E25.0");var subQ6=sQuery(id+"F0.wireOp",EDGE,"E25.2");var subQ7=sQuery(id+"F0.wireOp",EDGE,"E25.3");Q4=makeQuery(id+"F8.boolean.opBoolean","INTERSECT",EDGE,{"derivedFrom":[makeQuery(id+"F5.boolean.opBoolean","SPLIT",FACE,{"disambiguationData":[TD([makeQuery(id+"F2.opExtrude","SWEPT_FACE",FACE,{"disambiguationData":[OSD([subQ5])]})])],"derivedFrom":makeQuery(id+"F3.boolean.opBoolean","COPY",FACE,{"derivedFrom":makeQuery(id+"F3.opExtrude","CAP_FACE",FACE,{"disambiguationData":[OSD([subQ5,subQ1,subQ6,subQ7,subQ4,subQ3,subQ2,subQ0])],"isStart":false})})}),makeQuery(id+"F8.opExtrude","SWEPT_FACE",FACE,{"disambiguationData":[OSD([sQuery(id+"F7.wireOp",EDGE,"E67")])]})]});}
            var Q5;
            Q5=makeQuery(id+"F8.boolean.opBoolean","INTERSECT",EDGE,{"disambiguationData":[OD(0.0)],"derivedFrom":[makeQuery(id+"F5.opExtrude","SWEPT_FACE",FACE,{"disambiguationData":[OSD([sQuery(id+"F4.wireOp",EDGE,"E30")])]}),makeQuery(id+"F8.opExtrude","SWEPT_FACE",FACE,{"disambiguationData":[OSD([sQuery(id+"F7.wireOp",EDGE,"E67")])]})]});
            fillet(context, id + "F14", {"entities" : qUnion([Q0, Q1, Q2, Q3, Q4, Q5]), "radius" : 3 * mm, "tangentPropagation" : true, "allowEdgeOverflow" : false});
        }
        {
            var Q0;
            Q0=makeQuery(id+"F1.opExtrude","CAP_EDGE",EDGE,{"disambiguationData":[OSD([sQuery(id+"F0.wireOp",EDGE,"E1.bottom")])],"isStart":false});
            fillet(context, id + "F15", {"entities" : qUnion([Q0]), "radius" : 2 * mm, "tangentPropagation" : true, "allowEdgeOverflow" : false});
        }
        {
            var Q0;
            {var subQ0=sQuery(id+"F0.wireOp",EDGE,"E22.filletArc");var subQ1=sQuery(id+"F0.wireOp",EDGE,"E7");var subQ2=sQuery(id+"F0.wireOp",EDGE,"E6");var subQ3=sQuery(id+"F0.wireOp",EDGE,"E5");var subQ4=sQuery(id+"F0.wireOp",EDGE,"E4");var subQ5=sQuery(id+"F0.wireOp",EDGE,"E1.bottom");var subQ6=sQuery(id+"F0.wireOp",EDGE,"E21.filletArc");var subQ7=sQuery(id+"F0.wireOp",EDGE,"E1.top");var subQ8=sQuery(id+"F0.wireOp",EDGE,"E1.left");var subQ9=sQuery(id+"F0.wireOp",EDGE,"E1.right");var subQ10=sQuery(id+"F0.wireOp",EDGE,"E23.filletArc");var subQ11=sQuery(id+"F0.wireOp",EDGE,"E24.filletArc");Q0=makeQuery(id+"F2.boolean.opBoolean","SPLIT",FACE,{"disambiguationData":[TD([makeQuery(id+"F1.opExtrude","SWEPT_FACE",FACE,{"disambiguationData":[OSD([subQ5])]})])],"derivedFrom":makeQuery(id+"F1.opExtrude","CAP_FACE",FACE,{"disambiguationData":[OSD([subQ5,subQ7,subQ8,subQ9,subQ4,subQ3,subQ2,subQ1,subQ6,subQ0,subQ10,subQ11])],"isStart":true})});}
            var sketch = newSketch(context, id + "F16", { "sketchPlane" : qUnion([Q0])});
            skLineSegment(sketch, "E79", {"start": v(0, 90) * mm, "end": v(0, 120) * mm, "construction": true});
            skCircle(sketch, "E80", {"center": v(0, 120) * mm, "radius": 6 * mm});
            skArc(sketch, "E81", {"start": v(15, 120) * mm, "mid": v(0, 135) * mm, "end": v(-15, 120) * mm});
            skLineSegment(sketch, "E82", {"start": v(15, 120) * mm, "end": v(15, 108) * mm});
            skLineSegment(sketch, "E83", {"start": v(-15, 120) * mm, "end": v(-15, 108) * mm});
            skLineSegment(sketch, "E84", {"start": v(15, 108) * mm, "end": v(33, 90) * mm});
            skLineSegment(sketch, "E85", {"start": v(-15, 108) * mm, "end": v(-33, 90) * mm});
            skLineSegment(sketch, "E86", {"start": v(-80, 0) * mm, "end": v(80, 0) * mm, "construction": true});
            skLineSegment(sketch, "E87.MirrorCS", {"start": v(-15, -108) * mm, "end": v(-33, -90) * mm});
            skArc(sketch, "E88.MirrorCS", {"start": v(15, -120) * mm, "mid": v(0, -135) * mm, "end": v(-15, -120) * mm});
            skLineSegment(sketch, "E89.MirrorCS", {"start": v(-15, -120) * mm, "end": v(-15, -108) * mm});
            skCircle(sketch, "E90.MirrorC", {"center": v(0, -120) * mm, "radius": 6 * mm});
            skLineSegment(sketch, "E91.MirrorCS", {"start": v(0, -90) * mm, "end": v(0, -120) * mm, "construction": true});
            skLineSegment(sketch, "E92.MirrorCS", {"start": v(15, -108) * mm, "end": v(33, -90) * mm});
            skLineSegment(sketch, "E93.MirrorCS", {"start": v(15, -120) * mm, "end": v(15, -108) * mm});
            skSolve(sketch);
        }
        {
            var Q0;
            Q0=makeQuery(id+"F16.imprint","IMPRINT",FACE,{"disambiguationData":[TD([[makeQuery(id+"F16.imprint","IMPRINT",EDGE,{"derivedFrom":makeQuery(id+"F1.opExtrude","CAP_EDGE",EDGE,{"disambiguationData":[OSD([sQuery(id+"F0.wireOp",EDGE,"E1.left")])],"isStart":true})}),-1.0]])]});
            var Q1;
            Q1=makeQuery(id+"F16.imprint","IMPRINT",FACE,{"disambiguationData":[TD([[makeQuery(id+"F16.imprint","IMPRINT",EDGE,{"derivedFrom":sQuery(id+"F16.wireOp",EDGE,"E80")}),-1.0]])]});
            var Q2;
            {var subQ0=sQuery(id+"F16.wireOp",EDGE,"E87.MirrorCS");Q2=makeQuery(id+"F16.imprint","IMPRINT",FACE,{"disambiguationData":[TD([[makeQuery(id+"F16.imprint","IMPRINT",EDGE,{"derivedFrom":subQ0}),-1.0]])]});}
            extrude(context, id + "F17", {"entities" : qUnion([Q0, Q1, Q2]), "operationType" : NewBodyOperationType.ADD, "depth" : 3 * mm});
        }
    });
